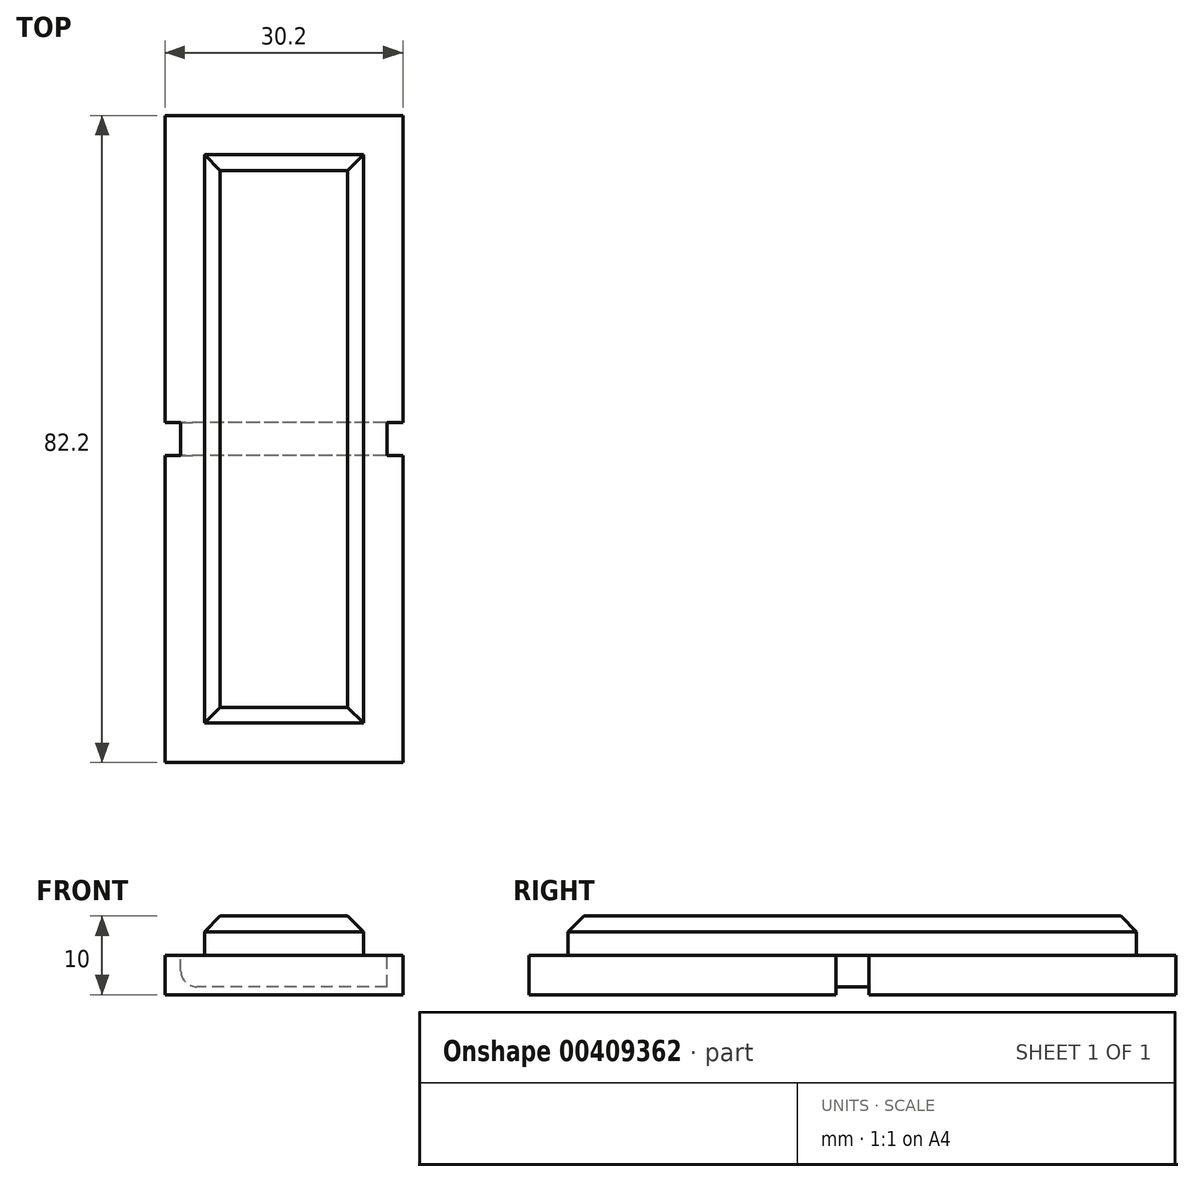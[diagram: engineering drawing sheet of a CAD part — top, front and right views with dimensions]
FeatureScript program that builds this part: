
annotation { "Feature Type Name" : "Feature", "Feature Type Description" : "" }
export const myFeature = defineFeature(function(context is Context, id is Id, definition is map)
    precondition{}
    {
        {
            var Q0;
            Q0=qCreatedBy(makeId("Top.planeOp"),FACE);
            var sketch = newSketch(context, id + "F0", { "sketchPlane" : qUnion([Q0])});
            skLineSegment(sketch, "E0.bottom", {"start": v(0, 0) * mm, "end": v(30.2, 0) * mm});
            skLineSegment(sketch, "E0.top", {"start": v(0, -82.2) * mm, "end": v(30.2, -82.2) * mm});
            skLineSegment(sketch, "E0.left", {"start": v(0, 0) * mm, "end": v(0, -82.2) * mm});
            skLineSegment(sketch, "E0.right", {"start": v(30.2, 0) * mm, "end": v(30.2, -82.2) * mm});
            skSolve(sketch);
        }
        {
            var Q0;
            Q0 = qSketchRegion(id + "F0", true);
            extrude(context, id + "F1", {"entities" : qUnion([Q0]), "depth" : 5 * mm});
        }
        {
            var Q0;
            Q0=makeQuery(id+"F1.opExtrude","CAP_FACE",FACE,{"disambiguationData":[OSD([sQuery(id+"F0.wireOp",EDGE,"E0.bottom"),sQuery(id+"F0.wireOp",EDGE,"E0.top"),sQuery(id+"F0.wireOp",EDGE,"E0.left"),sQuery(id+"F0.wireOp",EDGE,"E0.right")])],"isStart":false});
            var sketch = newSketch(context, id + "F2", { "sketchPlane" : qUnion([Q0])});
            skLineSegment(sketch, "E1.bottom", {"start": v(5, -5) * mm, "end": v(25.2, -5) * mm});
            skLineSegment(sketch, "E1.top", {"start": v(5, -77.2) * mm, "end": v(25.2, -77.2) * mm});
            skLineSegment(sketch, "E1.left", {"start": v(5, -5) * mm, "end": v(5, -77.2) * mm});
            skLineSegment(sketch, "E1.right", {"start": v(25.2, -5) * mm, "end": v(25.2, -77.2) * mm});
            skSolve(sketch);
        }
        {
            var Q0;
            Q0=makeQuery(id+"F2.imprint","IMPRINT",FACE,{"disambiguationData":[TD([[makeQuery(id+"F2.imprint","IMPRINT",EDGE,{"derivedFrom":sQuery(id+"F2.wireOp",EDGE,"E1.bottom")}),-1.0]])]});
            extrude(context, id + "F3", {"entities" : qUnion([Q0]), "operationType" : NewBodyOperationType.ADD, "depth" : 5 * mm});
        }
        {
            var Q0;
            Q0=makeQuery(id+"F3.opExtrude","CAP_FACE",FACE,{"disambiguationData":[OSD([sQuery(id+"F2.wireOp",EDGE,"E1.bottom"),sQuery(id+"F2.wireOp",EDGE,"E1.top"),sQuery(id+"F2.wireOp",EDGE,"E1.left"),sQuery(id+"F2.wireOp",EDGE,"E1.right")])],"isStart":false});
            chamfer(context, id + "F4", {"entities" : qUnion([Q0]), "width" : 2 * mm, "tangentPropagation" : true});
        }
        {
            var Q0;
            Q0=makeQuery(id+"F1.opExtrude","CAP_FACE",FACE,{"disambiguationData":[OSD([sQuery(id+"F0.wireOp",EDGE,"E0.bottom"),sQuery(id+"F0.wireOp",EDGE,"E0.top"),sQuery(id+"F0.wireOp",EDGE,"E0.left"),sQuery(id+"F0.wireOp",EDGE,"E0.right")])],"isStart":false});
            var sketch = newSketch(context, id + "F5", { "sketchPlane" : qUnion([Q0])});
            skLineSegment(sketch, "E2.bottom", {"start": v(0, -39) * mm, "end": v(2, -39) * mm});
            skLineSegment(sketch, "E2.top", {"start": v(0, -43.2) * mm, "end": v(2, -43.2) * mm});
            skLineSegment(sketch, "E2.left", {"start": v(0, -39) * mm, "end": v(0, -43.2) * mm});
            skLineSegment(sketch, "E2.right", {"start": v(2, -39) * mm, "end": v(2, -43.2) * mm});
            skLineSegment(sketch, "E3.bottom", {"start": v(30.2, -43.2) * mm, "end": v(28.2, -43.2) * mm});
            skLineSegment(sketch, "E3.top", {"start": v(30.2, -39) * mm, "end": v(28.2, -39) * mm});
            skLineSegment(sketch, "E3.left", {"start": v(30.2, -43.2) * mm, "end": v(30.2, -39) * mm});
            skLineSegment(sketch, "E3.right", {"start": v(28.2, -43.2) * mm, "end": v(28.2, -39) * mm});
            skSolve(sketch);
        }
        {
            var Q0;
            Q0 = qSketchRegion(id + "F5", true);
            extrude(context, id + "F6", {"entities" : qUnion([Q0]), "operationType" : NewBodyOperationType.REMOVE, "endBound" : BoundingType.UP_TO_NEXT, "oppositeDirection" : true, "depth" : 25 * mm});
        }
        {
            var Q0;
            Q0=qCreatedBy(makeId("Right.planeOp"),FACE);
            var sketch = newSketch(context, id + "F7", { "sketchPlane" : qUnion([Q0])});
            skLineSegment(sketch, "E4.bottom", {"start": v(-43.2, 1) * mm, "end": v(-39, 1) * mm});
            skLineSegment(sketch, "E4.top", {"start": v(-43.2, 0) * mm, "end": v(-39, 0) * mm});
            skLineSegment(sketch, "E4.left", {"start": v(-43.2, 1) * mm, "end": v(-43.2, 0) * mm});
            skLineSegment(sketch, "E4.right", {"start": v(-39, 1) * mm, "end": v(-39, 0) * mm});
            skSolve(sketch);
        }
        {
            var Q0;
            Q0 = qSketchRegion(id + "F7", true);
            var Q1;
            Q1=makeQuery(id+"F6.boolean.opBoolean","COPY",FACE,{"derivedFrom":makeQuery(id+"F6.opExtrude","SWEPT_FACE",FACE,{"disambiguationData":[OSD([sQuery(id+"F5.wireOp",EDGE,"E3.right")])]})});
            extrude(context, id + "F8", {"entities" : qUnion([Q0]), "operationType" : NewBodyOperationType.REMOVE, "endBound" : BoundingType.UP_TO_SURFACE, "endBoundEntityFace" : qUnion([Q1]), "depth" : 30.8 * mm});
        }
        {
            var Q0;
            Q0=makeQuery(id+"F8.boolean.opBoolean","INTERSECT",EDGE,{"derivedFrom":[makeQuery(id+"F6.boolean.opBoolean","COPY",FACE,{"derivedFrom":makeQuery(id+"F6.opExtrude","SWEPT_FACE",FACE,{"disambiguationData":[OSD([sQuery(id+"F5.wireOp",EDGE,"E2.right")])]})}),makeQuery(id+"F8.opExtrude","SWEPT_FACE",FACE,{"disambiguationData":[OSD([sQuery(id+"F7.wireOp",EDGE,"E4.bottom")])]})]});
            var Q1;
            Q1=makeQuery(id+"F8.boolean.opBoolean","COPY",EDGE,{"derivedFrom":makeQuery(id+"F8.opExtrude","CAP_EDGE",EDGE,{"disambiguationData":[OSD([sQuery(id+"F7.wireOp",EDGE,"E4.bottom")])],"isStart":false})});
            fillet(context, id + "F9", {"entities" : qUnion([Q0, Q1]), "radius" : 2 * mm, "tangentPropagation" : true, "allowEdgeOverflow" : false});
        }
    });
